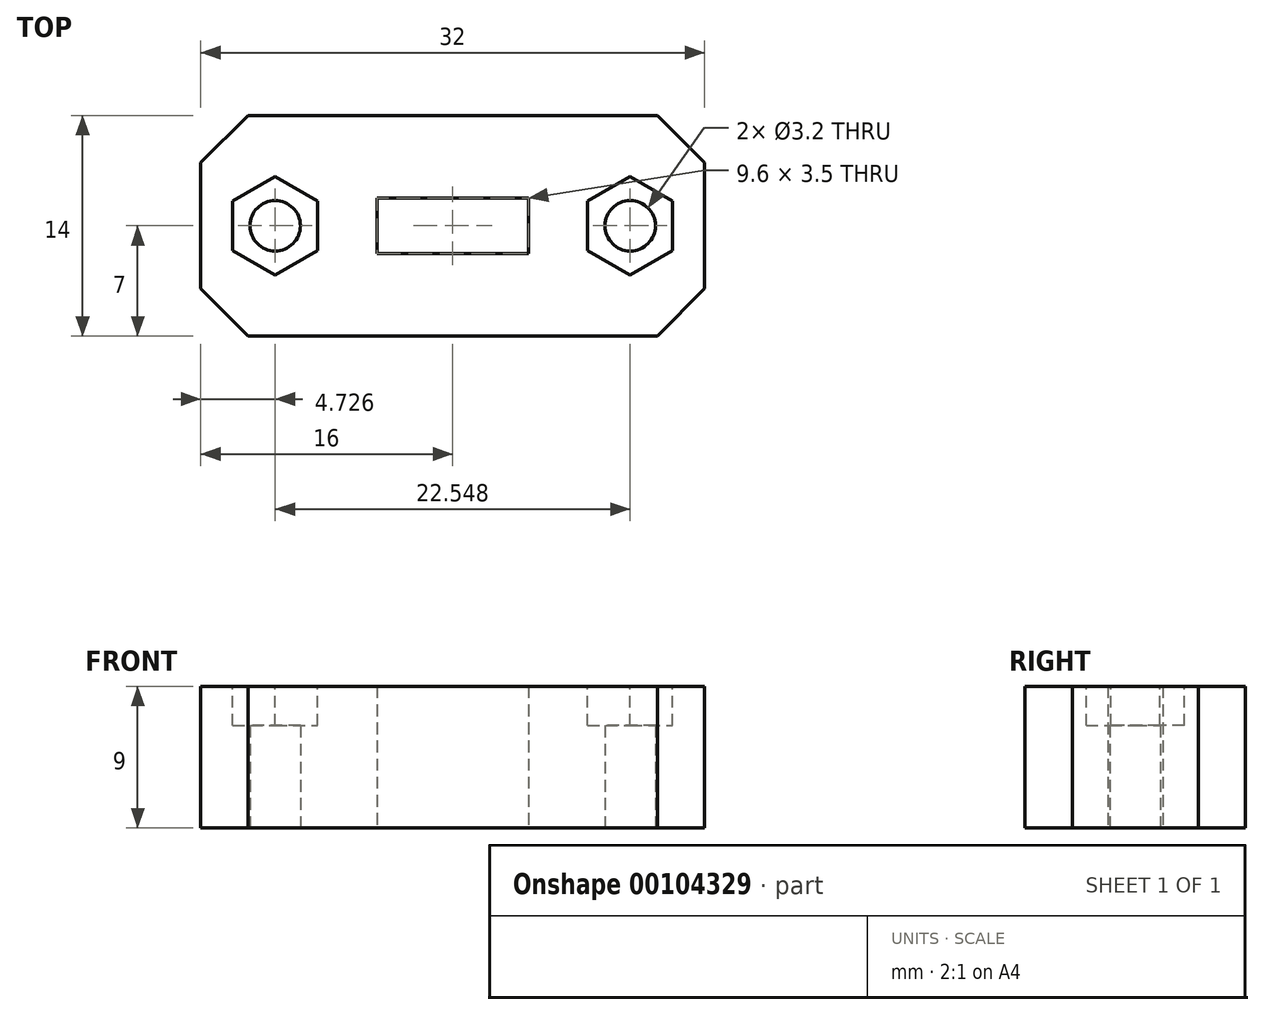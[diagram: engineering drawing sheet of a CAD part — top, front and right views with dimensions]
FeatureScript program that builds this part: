
annotation { "Feature Type Name" : "Feature", "Feature Type Description" : "" }
export const myFeature = defineFeature(function(context is Context, id is Id, definition is map)
    precondition{}
    {
        {
            var Q0;
            Q0=qCreatedBy(makeId("Top.planeOp"),FACE);
            var sketch = newSketch(context, id + "F0", { "sketchPlane" : qUnion([Q0])});
            skLineSegment(sketch, "E0.bottom", {"start": v(16, -4.95) * mm, "end": v(-16, -4.95) * mm});
            skLineSegment(sketch, "E0.top", {"start": v(16, 9.05) * mm, "end": v(-16, 9.05) * mm});
            skLineSegment(sketch, "E0.left", {"start": v(16, -4.95) * mm, "end": v(16, 9.05) * mm});
            skLineSegment(sketch, "E0.right", {"start": v(-16, -4.95) * mm, "end": v(-16, 9.05) * mm});
            skLineSegment(sketch, "E1.bottom", {"start": v(-4.8, 3.8) * mm, "end": v(4.8, 3.8) * mm});
            skLineSegment(sketch, "E1.top", {"start": v(-4.8, 0.3) * mm, "end": v(4.8, 0.3) * mm});
            skLineSegment(sketch, "E1.left", {"start": v(-4.8, 3.8) * mm, "end": v(-4.8, 0.3) * mm});
            skLineSegment(sketch, "E1.right", {"start": v(4.8, 3.8) * mm, "end": v(4.8, 0.3) * mm});
            skCircle(sketch, "E2", {"center": v(-11.27, 2.05) * mm, "radius": 1.6 * mm});
            skCircle(sketch, "E3", {"center": v(11.27, 2.05) * mm, "radius": 1.6 * mm});
            skSolve(sketch);
        }
        {
            var Q0;
            Q0 = qSketchRegion(id + "F0", true);
            extrude(context, id + "F1", {"entities" : qUnion([Q0]), "depth" : 9 * mm});
        }
        {
            var Q0;
            Q0=makeQuery(id+"F1.opExtrude","SWEPT_EDGE",EDGE,{"disambiguationData":[OSD([sQuery(id+"F0.wireOp",EDGE,"E0.bottom"),sQuery(id+"F0.wireOp",EDGE,"E0.right")])]});
            var Q1;
            Q1=makeQuery(id+"F1.opExtrude","SWEPT_EDGE",EDGE,{"disambiguationData":[OSD([sQuery(id+"F0.wireOp",EDGE,"E0.bottom"),sQuery(id+"F0.wireOp",EDGE,"E0.left")])]});
            var Q2;
            Q2=makeQuery(id+"F1.opExtrude","SWEPT_EDGE",EDGE,{"disambiguationData":[OSD([sQuery(id+"F0.wireOp",EDGE,"E0.top"),sQuery(id+"F0.wireOp",EDGE,"E0.left")])]});
            var Q3;
            Q3=makeQuery(id+"F1.opExtrude","SWEPT_EDGE",EDGE,{"disambiguationData":[OSD([sQuery(id+"F0.wireOp",EDGE,"E0.top"),sQuery(id+"F0.wireOp",EDGE,"E0.right")])]});
            chamfer(context, id + "F2", {"entities" : qUnion([Q0, Q1, Q2, Q3]), "width" : 3 * mm, "tangentPropagation" : true});
        }
        {
            var Q0;
            Q0=makeQuery(id+"F1.opExtrude","CAP_FACE",FACE,{"disambiguationData":[OSD([sQuery(id+"F0.wireOp",EDGE,"E0.bottom"),sQuery(id+"F0.wireOp",EDGE,"E0.top"),sQuery(id+"F0.wireOp",EDGE,"E0.left"),sQuery(id+"F0.wireOp",EDGE,"E0.right"),sQuery(id+"F0.wireOp",EDGE,"E1.bottom"),sQuery(id+"F0.wireOp",EDGE,"E1.top"),sQuery(id+"F0.wireOp",EDGE,"E1.left"),sQuery(id+"F0.wireOp",EDGE,"E1.right"),sQuery(id+"F0.wireOp",EDGE,"E2"),sQuery(id+"F0.wireOp",EDGE,"E3")])],"isStart":false});
            var sketch = newSketch(context, id + "F3", { "sketchPlane" : qUnion([Q0])});
            skCircle(sketch, "E4.cCircle", {"center": v(-11.27, 2.05) * mm, "radius": 2.7 * mm, "construction": true});
            skLineSegment(sketch, "E4.0", {"start": v(-8.57, 3.6) * mm, "end": v(-8.57, 0.5) * mm});
            skLineSegment(sketch, "E4.1", {"start": v(-8.57, 0.5) * mm, "end": v(-11.27, -1.07) * mm});
            skLineSegment(sketch, "E4.2", {"start": v(-11.27, -1.07) * mm, "end": v(-13.97, 0.5) * mm});
            skLineSegment(sketch, "E4.3", {"start": v(-13.97, 0.5) * mm, "end": v(-13.97, 3.6) * mm});
            skLineSegment(sketch, "E4.4", {"start": v(-13.97, 3.6) * mm, "end": v(-11.27, 5.17) * mm});
            skLineSegment(sketch, "E4.5", {"start": v(-11.27, 5.17) * mm, "end": v(-8.57, 3.6) * mm});
            skPoint(sketch, "E4.0.midPoint", {"position": v(-8.57, 2.05) * mm});
            skCircle(sketch, "E5.cCircle", {"center": v(11.27, 2.05) * mm, "radius": 2.7 * mm, "construction": true});
            skLineSegment(sketch, "E5.0", {"start": v(13.97, 3.6) * mm, "end": v(13.97, 0.5) * mm});
            skLineSegment(sketch, "E5.1", {"start": v(13.97, 0.5) * mm, "end": v(11.27, -1.07) * mm});
            skLineSegment(sketch, "E5.2", {"start": v(11.27, -1.07) * mm, "end": v(8.57, 0.5) * mm});
            skLineSegment(sketch, "E5.3", {"start": v(8.57, 0.5) * mm, "end": v(8.57, 3.6) * mm});
            skLineSegment(sketch, "E5.4", {"start": v(8.57, 3.6) * mm, "end": v(11.27, 5.17) * mm});
            skLineSegment(sketch, "E5.5", {"start": v(11.27, 5.17) * mm, "end": v(13.97, 3.6) * mm});
            skPoint(sketch, "E5.0.midPoint", {"position": v(13.97, 2.05) * mm});
            skSolve(sketch);
        }
        {
            var Q0;
            Q0 = qSketchRegion(id + "F3", true);
            extrude(context, id + "F4", {"entities" : qUnion([Q0]), "operationType" : NewBodyOperationType.REMOVE, "oppositeDirection" : true, "depth" : 2.5 * mm});
        }
    });
